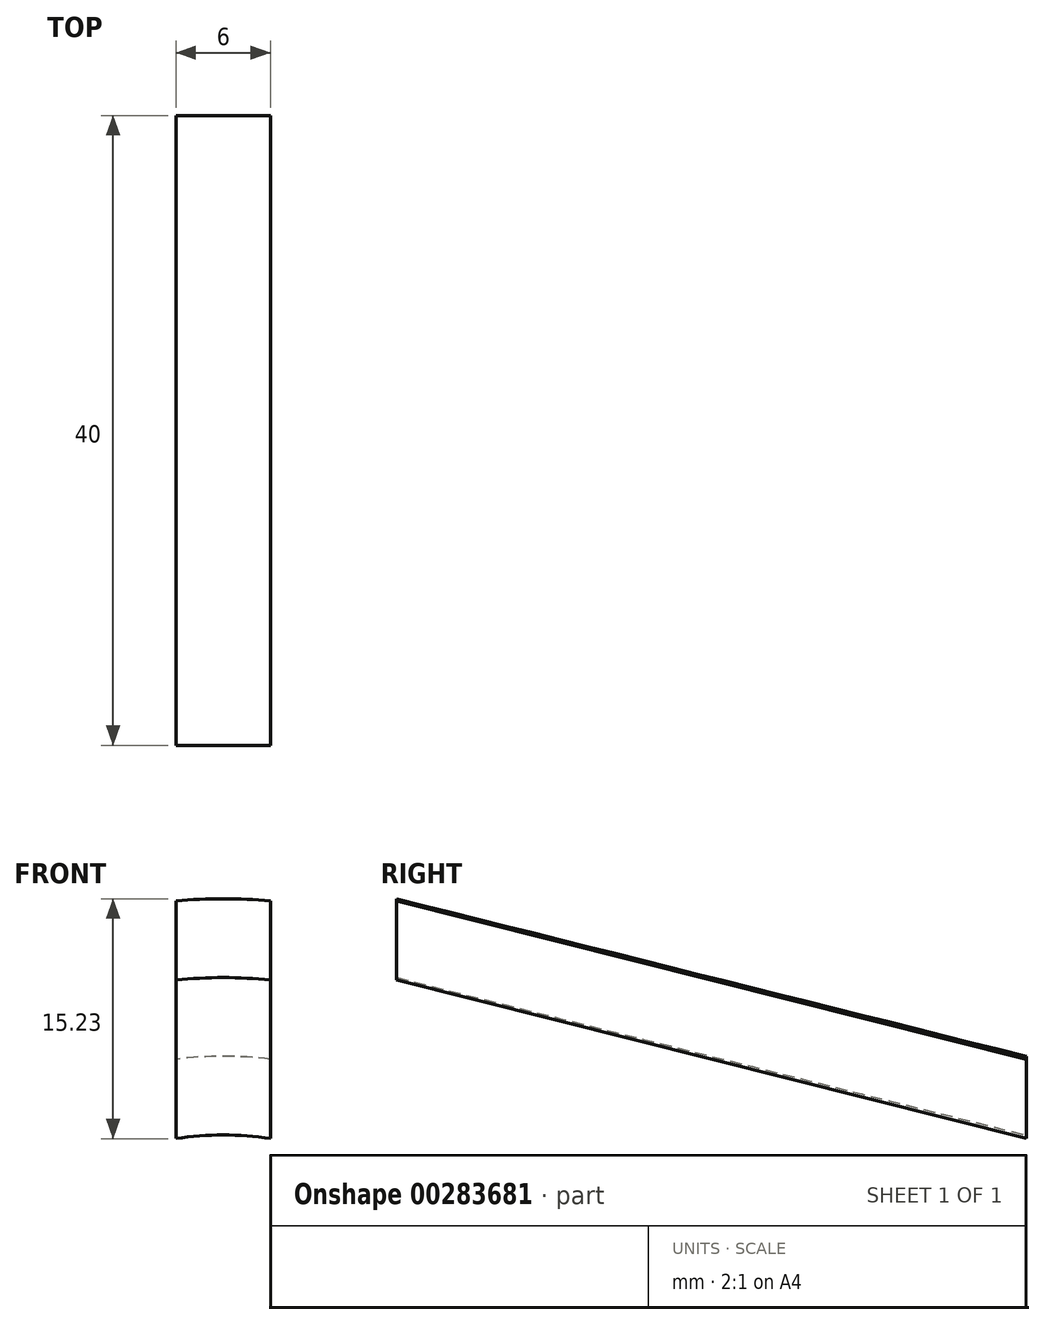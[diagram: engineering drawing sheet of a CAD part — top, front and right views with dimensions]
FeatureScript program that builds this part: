
annotation { "Feature Type Name" : "Feature", "Feature Type Description" : "" }
export const myFeature = defineFeature(function(context is Context, id is Id, definition is map)
    precondition{}
    {
        {
            var Q0;
            Q0=qCreatedBy(makeId("Front.planeOp"),FACE);
            var sketch = newSketch(context, id + "F0", { "sketchPlane" : qUnion([Q0])});
            skCircle(sketch, "E0", {"center": v(0, 0) * mm, "radius": 20 * mm});
            skCircle(sketch, "E1", {"center": v(0, 0) * mm, "radius": 25 * mm});
            skLineSegment(sketch, "E2", {"start": v(-3, 24.82) * mm, "end": v(-3, 19.77) * mm});
            skLineSegment(sketch, "E3", {"start": v(3, 24.82) * mm, "end": v(3, 19.77) * mm});
            skLineSegment(sketch, "E4.1.0", {"start": v(-20, 15) * mm, "end": v(-15.62, 12.48) * mm});
            skLineSegment(sketch, "E4.1.1", {"start": v(-23, 9.81) * mm, "end": v(-18.62, 7.29) * mm});
            skLineSegment(sketch, "E4.2.0", {"start": v(-23, -9.81) * mm, "end": v(-18.62, -7.29) * mm});
            skLineSegment(sketch, "E4.2.1", {"start": v(-20, -15) * mm, "end": v(-15.62, -12.48) * mm});
            skLineSegment(sketch, "E4.3.0", {"start": v(-3, -24.82) * mm, "end": v(-3, -19.77) * mm});
            skLineSegment(sketch, "E4.3.1", {"start": v(3, -24.82) * mm, "end": v(3, -19.77) * mm});
            skLineSegment(sketch, "E4.4.0", {"start": v(20, -15) * mm, "end": v(15.62, -12.48) * mm});
            skLineSegment(sketch, "E4.4.1", {"start": v(23, -9.81) * mm, "end": v(18.62, -7.29) * mm});
            skLineSegment(sketch, "E4.5.0", {"start": v(23, 9.81) * mm, "end": v(18.62, 7.29) * mm});
            skLineSegment(sketch, "E4.5.1", {"start": v(20, 15) * mm, "end": v(15.62, 12.48) * mm});
            skSolve(sketch);
        }
        {
            var Q0;
            Q0=qCreatedBy(makeId("Front.planeOp"),FACE);
            cPlane(context, id + "F1", {"entities" : qUnion([Q0]), "cplaneType" : CPlaneType.OFFSET, "offset" : 40 * mm, "width" : 150 * mm, "height" : 150 * mm});
        }
        {
            var Q0;
            Q0=qCreatedBy(id+"F1.planeOp",FACE);
            var sketch = newSketch(context, id + "F2", { "sketchPlane" : qUnion([Q0])});
            skCircle(sketch, "E5", {"center": v(0, 0) * mm, "radius": 30 * mm});
            skCircle(sketch, "E6", {"center": v(0, 0) * mm, "radius": 35 * mm});
            skLineSegment(sketch, "E7", {"start": v(-3, 34.87) * mm, "end": v(-3, 29.85) * mm});
            skLineSegment(sketch, "E8", {"start": v(3, 29.85) * mm, "end": v(3, 34.87) * mm});
            skLineSegment(sketch, "E9.1.0", {"start": v(-24.35, 17.52) * mm, "end": v(-28.7, 20.03) * mm});
            skLineSegment(sketch, "E9.1.1", {"start": v(-31.7, 14.84) * mm, "end": v(-27.35, 12.33) * mm});
            skLineSegment(sketch, "E9.2.0", {"start": v(-27.35, -12.33) * mm, "end": v(-31.7, -14.84) * mm});
            skLineSegment(sketch, "E9.2.1", {"start": v(-28.7, -20.03) * mm, "end": v(-24.35, -17.52) * mm});
            skLineSegment(sketch, "E9.3.0", {"start": v(-3, -29.85) * mm, "end": v(-3, -34.87) * mm});
            skLineSegment(sketch, "E9.3.1", {"start": v(3, -34.87) * mm, "end": v(3, -29.85) * mm});
            skLineSegment(sketch, "E9.4.0", {"start": v(24.35, -17.52) * mm, "end": v(28.7, -20.03) * mm});
            skLineSegment(sketch, "E9.4.1", {"start": v(31.7, -14.84) * mm, "end": v(27.35, -12.33) * mm});
            skLineSegment(sketch, "E9.5.0", {"start": v(27.35, 12.33) * mm, "end": v(31.7, 14.84) * mm});
            skLineSegment(sketch, "E9.5.1", {"start": v(28.7, 20.03) * mm, "end": v(24.35, 17.52) * mm});
            skSolve(sketch);
        }
        {
            var Q0;
            {var subQ0=sQuery(id+"F0.wireOp",EDGE,"E2");Q0=makeQuery(id+"F0.imprint","IMPRINT",FACE,{"disambiguationData":[TD([[makeQuery(id+"F0.imprint","IMPRINT",EDGE,{"derivedFrom":subQ0}),1.0]])]});}
            var Q1;
            {var subQ0=sQuery(id+"F2.wireOp",EDGE,"E7");Q1=makeQuery(id+"F2.imprint","IMPRINT",FACE,{"disambiguationData":[TD([[makeQuery(id+"F2.imprint","IMPRINT",EDGE,{"derivedFrom":subQ0}),1.0]])]});}
            loft(context, id + "F3", {"sheetProfilesArray" : [{ "sheetProfileEntities" : qUnion([Q0]) }, { "sheetProfileEntities" : qUnion([Q1]) }]});
        }
    });
